FCSTD DOCUMENT  (FreeCAD 1.0R39319 (Git))
Label: Spec
License: All rights reserved
LicenseURL: https://en.wikipedia.org/wiki/All_rights_reserved
objects: Spreadsheet::Sheet×1

FEATURE [Spreadsheet::Sheet] Spreadsheet  label="Vars"
  cells = A1='Common; A2='clearance; B2(clearance)=0.2; A3='nut_inserts_m2; B3(nut_inserts_m2)=3.5; A4='nut_inserts_m3; B4(nut_inserts_m3)=4.5; A5='wall; B5(wall)=2.5; A6='ext_radius; B6(ext_radius)=10; A7='hood_angle; B7(hood_angle)=4; A12='Display; A13='display_width; B13(display_width)=231.3; A14='display_height; B14(display_height)=64.3; A15='display_depth; B15(display_depth)=5.5; A16='display_offset_bottom; B16(display_offset_bottom)==3 + display_view_offset; C16='display_view_offset; D16(display_view_offset)=1; A17='display_offset_left; B17(display_offset_left)==2.5 + display_view_offset; A18='display_offset_right; B18(display_offset_right)==7.5 + display_view_offset; A19='display_offset_top; B19(display_offset_top)==3 + display_view_offset; F20='b; A21='Top Enclosure; A22='top_enclosure_width; B22(top_enclosure_width)=280; A23='top_enclosure_height; B23(top_enclosure_height)=100; A24='top_enclosure_front_depth; B24(top_enclosure_front_depth)=1; A25='top_enclosure_back_depth; B25(top_enclosure_back_depth)==wall; A26='top_enclosure_display_back_depth; B26(top_enclosure_display_back_depth)=1; A27='top_enclosure_depth; B27(top_enclosure_depth)=14; A28='top_enclosure_internal_depth; B28(top_enclosure_internal_depth)==top_enclosure_depth - top_enclosure_front_depth - display_depth - top_enclosure_display_back_depth - top_enclosure_back_depth + wall; A30='Bottom Enclosure; A31='bottom_enclosure_width; B31(bottom_enclosure_width)==top_enclosure_width; A32='bottom_enclosure_height; B32(bottom_enclosure_height)=160; A33='bottom_enclosure_depth; B33(bottom_enclosure_depth)=30; A35='Keyboard Plate; A36='keyboard_plate_width; B36(keyboard_plate_width)==235 - 2; A37='keyboard_plate_height; B37(keyboard_plate_height)==82.5 - 2; A38='keyboard_plate_radius; B38(kayboard_plate_radius)==ext_radius / 2; A40='Keyboard Plate; A41='wire_hole_offset_x; B41(wire_hole_offset_x)=40; A42='wire_hole_width; B42(wire_hole_width)=30; A43='wire_hole_height; B43(wire_hole_height)=9
